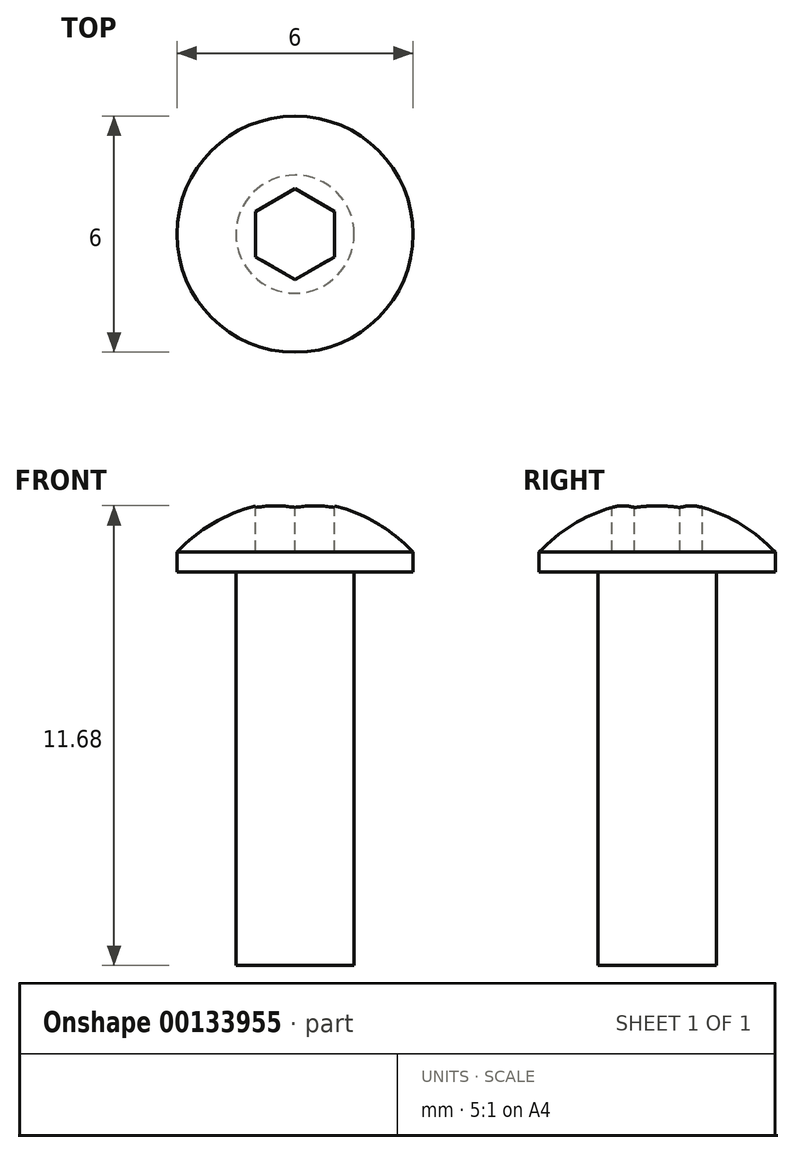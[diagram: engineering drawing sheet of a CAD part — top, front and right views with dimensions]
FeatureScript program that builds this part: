
annotation { "Feature Type Name" : "Feature", "Feature Type Description" : "" }
export const myFeature = defineFeature(function(context is Context, id is Id, definition is map)
    precondition{}
    {
        {
            var Q0;
            Q0=qCreatedBy(makeId("Front.planeOp"),FACE);
            var sketch = newSketch(context, id + "F0", { "sketchPlane" : qUnion([Q0])});
            skLineSegment(sketch, "E0", {"start": v(0, 11.74) * mm, "end": v(0, -9.83) * mm, "construction": true});
            skLineSegment(sketch, "E1", {"start": v(0, 0) * mm, "end": v(1.5, 0) * mm});
            skLineSegment(sketch, "E2", {"start": v(1.5, 0) * mm, "end": v(1.5, 10) * mm});
            skLineSegment(sketch, "E3", {"start": v(1.5, 10) * mm, "end": v(3, 10) * mm});
            skLineSegment(sketch, "E4", {"start": v(3, 10) * mm, "end": v(3, 10.5) * mm});
            skArc(sketch, "E5", {"start": v(3, 10.5) * mm, "mid": v(1.63, 11.46) * mm, "end": v(0, 11.8) * mm});
            skLineSegment(sketch, "E6", {"start": v(0, 11.8) * mm, "end": v(0, 0) * mm});
            skSolve(sketch);
        }
        {
            var Q0;
            Q0=qSketchRegion(id+"F0",true);
            var Q1;
            Q1=sQuery(id+"F0.wireOp",EDGE,"E0");
            revolve(context, id + "F1", {"surfaceOperationType" : NewSurfaceOperationType.NEW, "entities" : qUnion([Q0]), "axis" : qUnion([Q1]), "revolveType" : RevolveType.FULL});
        }
        {
            var Q0;
            Q0=qCreatedBy(makeId("Top.planeOp"),FACE);
            cPlane(context, id + "F2", {"entities" : qUnion([Q0]), "cplaneType" : CPlaneType.OFFSET, "offset" : 13 * mm, "width" : 150 * mm, "height" : 150 * mm});
        }
        {
            var Q0;
            Q0=qCreatedBy(id+"F2.planeOp",FACE);
            var sketch = newSketch(context, id + "F3", { "sketchPlane" : qUnion([Q0])});
            skCircle(sketch, "E7.cCircle", {"center": v(0, 0) * mm, "radius": 1 * mm, "construction": true});
            skLineSegment(sketch, "E7.0", {"start": v(1, 0.58) * mm, "end": v(1, -0.58) * mm});
            skLineSegment(sketch, "E7.1", {"start": v(1, -0.58) * mm, "end": v(0, -1.15) * mm});
            skLineSegment(sketch, "E7.2", {"start": v(0, -1.15) * mm, "end": v(-1, -0.58) * mm});
            skLineSegment(sketch, "E7.3", {"start": v(-1, -0.58) * mm, "end": v(-1, 0.58) * mm});
            skLineSegment(sketch, "E7.4", {"start": v(-1, 0.58) * mm, "end": v(0, 1.15) * mm});
            skLineSegment(sketch, "E7.5", {"start": v(0, 1.15) * mm, "end": v(1, 0.58) * mm});
            skPoint(sketch, "E7.0.midPoint", {"position": v(1, 0) * mm});
            skSolve(sketch);
        }
        {
            var Q0;
            Q0=qSketchRegion(id+"F3",true);
            extrude(context, id + "F4", {"entities" : qUnion([Q0]), "operationType" : NewBodyOperationType.REMOVE, "oppositeDirection" : true, "depth" : 2.5 * mm, "offsetDistance" : 25 * mm});
        }
    });
